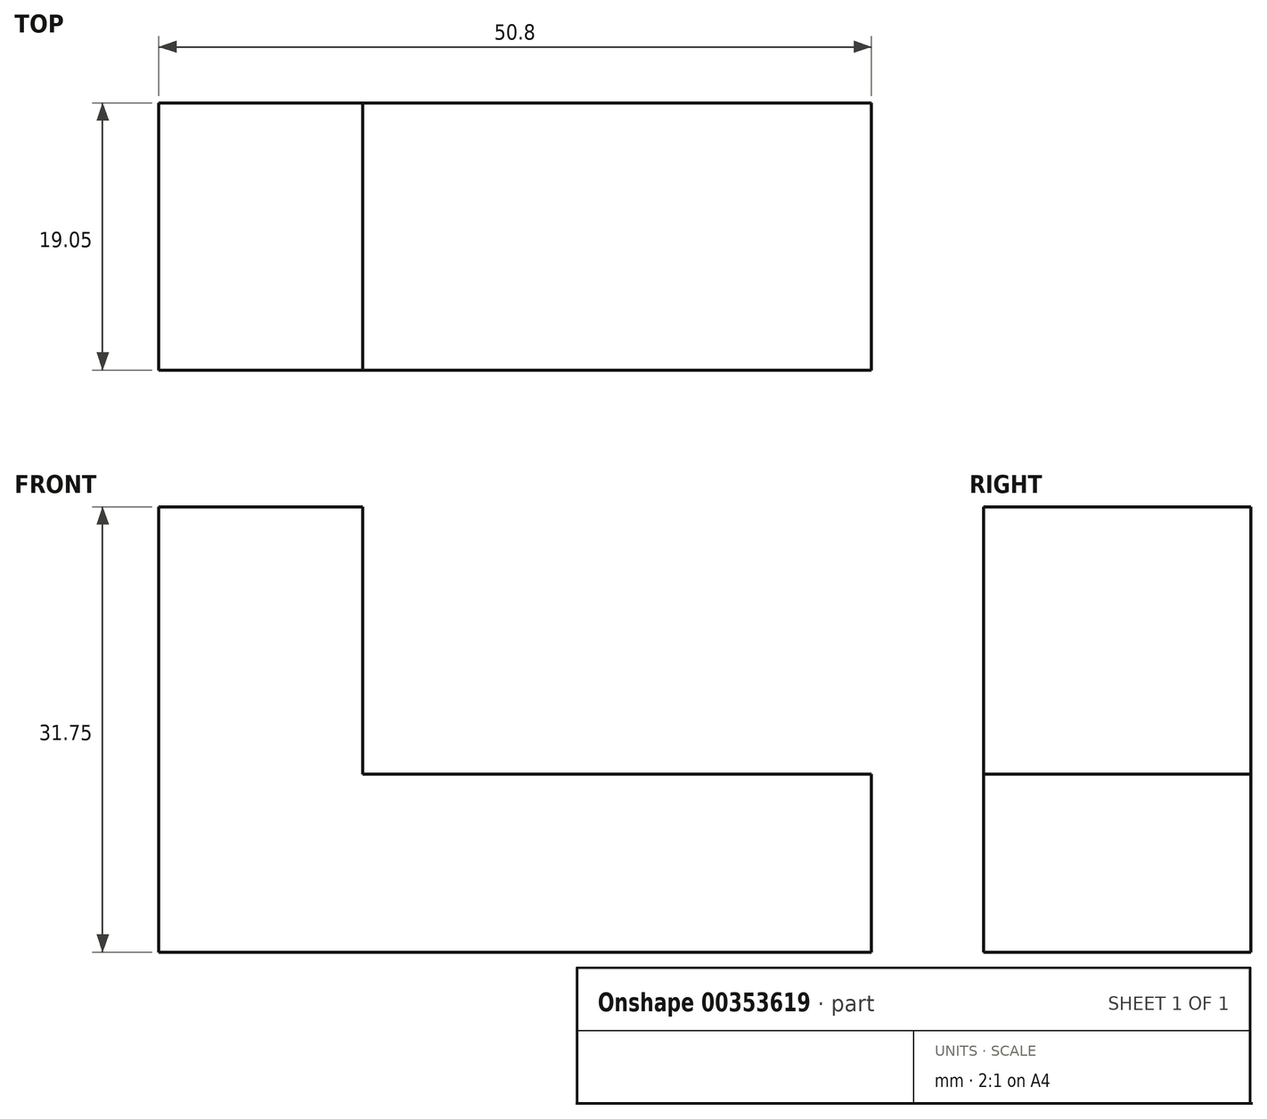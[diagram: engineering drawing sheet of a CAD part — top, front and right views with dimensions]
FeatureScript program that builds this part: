
annotation { "Feature Type Name" : "Feature", "Feature Type Description" : "" }
export const myFeature = defineFeature(function(context is Context, id is Id, definition is map)
    precondition{}
    {
        {
            var Q0;
            Q0=qCreatedBy(makeId("Front.planeOp"),FACE);
            var sketch = newSketch(context, id + "F0", { "sketchPlane" : qUnion([Q0])});
            skLineSegment(sketch, "E0", {"start": v(8.67, 0) * mm, "end": v(8.67, 31.75) * mm});
            skLineSegment(sketch, "E1", {"start": v(8.67, 31.75) * mm, "end": v(23.21, 31.75) * mm});
            skLineSegment(sketch, "E2", {"start": v(23.21, 31.75) * mm, "end": v(23.21, 12.7) * mm});
            skLineSegment(sketch, "E3", {"start": v(23.21, 12.7) * mm, "end": v(59.47, 12.7) * mm});
            skLineSegment(sketch, "E4", {"start": v(59.47, 12.7) * mm, "end": v(59.47, 0) * mm});
            skLineSegment(sketch, "E5", {"start": v(59.47, 0) * mm, "end": v(8.67, 0) * mm});
            skSolve(sketch);
        }
        {
            var Q0;
            Q0=makeQuery(id+"F0.imprint","IMPRINT",FACE,{"disambiguationData":[TD([[makeQuery(id+"F0.imprint","IMPRINT",EDGE,{"derivedFrom":sQuery(id+"F0.wireOp",EDGE,"E0")}),-1.0]])]});
            extrude(context, id + "F1", {"entities" : qUnion([Q0]), "depth" : 19.05 * mm});
        }
    });
